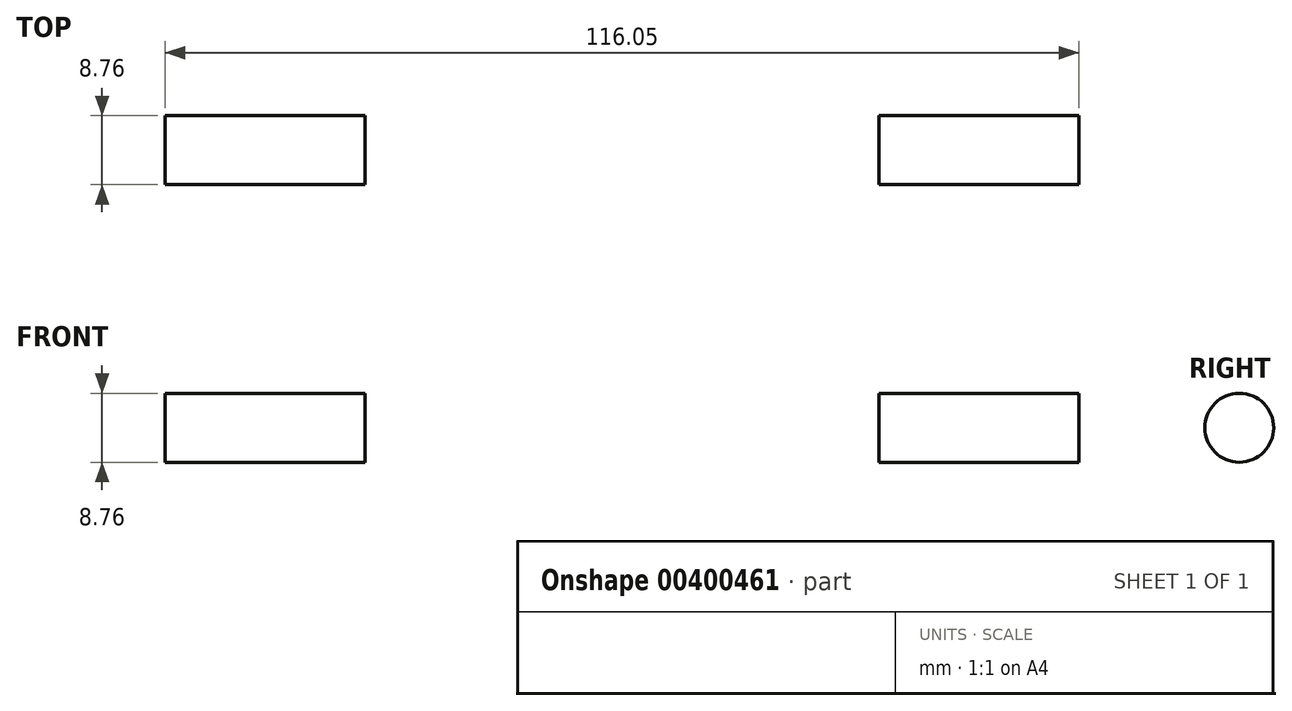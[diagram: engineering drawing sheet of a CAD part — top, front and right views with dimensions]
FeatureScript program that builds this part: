
annotation { "Feature Type Name" : "Feature", "Feature Type Description" : "" }
export const myFeature = defineFeature(function(context is Context, id is Id, definition is map)
    precondition{}
    {
        {
            var Q0;
            Q0=qCreatedBy(makeId("Front.planeOp"),FACE);
            var sketch = newSketch(context, id + "F0", { "sketchPlane" : qUnion([Q0])});
            skLineSegment(sketch, "E0", {"start": v(-62.11, 36.95) * mm, "end": v(-36.71, 36.95) * mm});
            skLineSegment(sketch, "E1", {"start": v(-62.11, 36.95) * mm, "end": v(-62.11, 32.57) * mm});
            skLineSegment(sketch, "E2", {"start": v(-62.11, 32.57) * mm, "end": v(-36.71, 32.57) * mm});
            skLineSegment(sketch, "E3", {"start": v(-36.71, 32.57) * mm, "end": v(-36.71, 36.95) * mm});
            skLineSegment(sketch, "E4", {"start": v(28.54, 36.95) * mm, "end": v(53.94, 36.95) * mm});
            skLineSegment(sketch, "E5", {"start": v(53.94, 36.95) * mm, "end": v(53.94, 32.57) * mm});
            skLineSegment(sketch, "E6", {"start": v(53.94, 32.57) * mm, "end": v(28.54, 32.57) * mm});
            skLineSegment(sketch, "E7", {"start": v(28.54, 32.57) * mm, "end": v(28.54, 36.95) * mm});
            skSolve(sketch);
        }
        {
            var Q0;
            Q0 = qSketchRegion(id + "F0", true);
            var Q1;
            Q1=sQuery(id+"F0.wireOp",EDGE,"E2");
            revolve(context, id + "F1", {"entities" : qUnion([Q0]), "axis" : qUnion([Q1]), "revolveType" : RevolveType.FULL});
        }
    });
